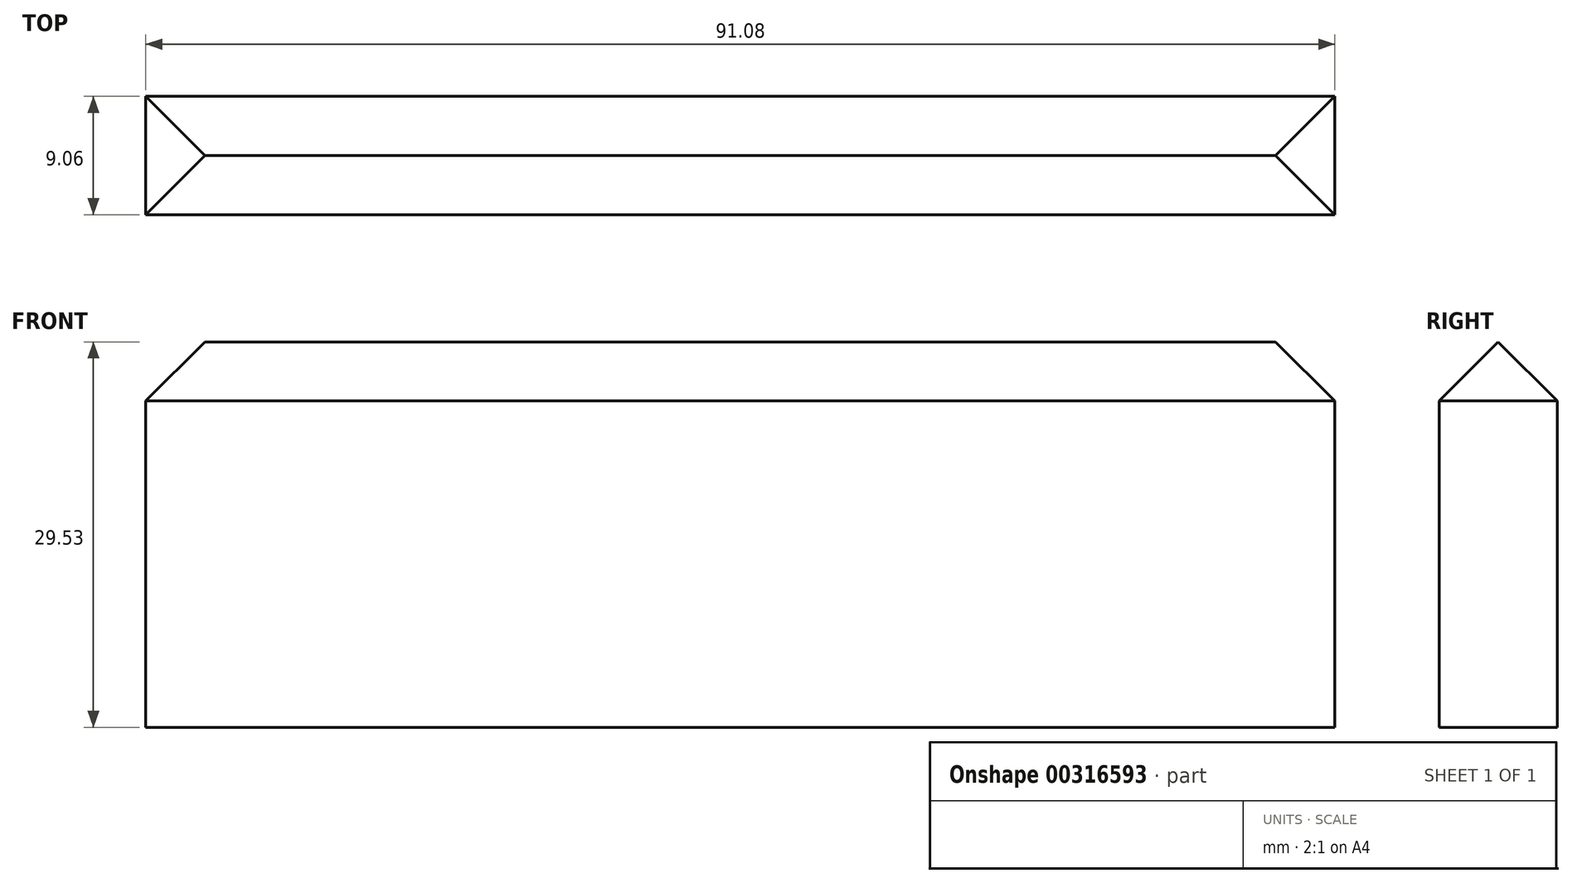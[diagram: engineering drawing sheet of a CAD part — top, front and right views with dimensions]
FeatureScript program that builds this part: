
annotation { "Feature Type Name" : "Feature", "Feature Type Description" : "" }
export const myFeature = defineFeature(function(context is Context, id is Id, definition is map)
    precondition{}
    {
        {
            var Q0;
            Q0=qCreatedBy(makeId("Top.planeOp"),FACE);
            var sketch = newSketch(context, id + "F0", { "sketchPlane" : qUnion([Q0])});
            skLineSegment(sketch, "E0.bottom", {"start": v(-43.93, 37.14) * mm, "end": v(47.15, 37.14) * mm});
            skLineSegment(sketch, "E0.top", {"start": v(-43.93, 46.2) * mm, "end": v(47.15, 46.2) * mm});
            skLineSegment(sketch, "E0.left", {"start": v(-43.93, 46.2) * mm, "end": v(-43.93, 37.14) * mm});
            skLineSegment(sketch, "E0.right", {"start": v(47.15, 46.2) * mm, "end": v(47.15, 37.14) * mm});
            skSolve(sketch);
        }
        {
            var Q0;
            Q0=makeQuery(id+"F0.imprint","IMPRINT",FACE,{"disambiguationData":[TD([[makeQuery(id+"F0.imprint","IMPRINT",EDGE,{"derivedFrom":sQuery(id+"F0.wireOp",EDGE,"E0.bottom")}),1.0]])]});
            extrude(context, id + "F1", {"entities" : qUnion([Q0]), "depth" : 15 * mm, "hasDraft" : true, "draftAngle" : 45 * degree, "draftPullDirection" : true, "hasSecondDirection" : true, "secondDirectionOppositeDirection" : true, "secondDirectionDepth" : 25 * mm});
        }
    });
